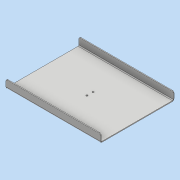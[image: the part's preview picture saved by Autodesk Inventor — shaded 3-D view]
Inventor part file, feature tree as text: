
AUTODESK INVENTOR PART (.ipt)
format: ipt  version: 2018 (Build 220112000, 112)  size: 156,160 bytes
history: native  units: mm
features: other x13, reference x6, sketch x3, hole x1
ambient origin geometry x8: Origin, YZ Plane, XZ Plane, XY Plane, X Axis, Y Axis, Z Axis, Center Point
bodies: Volumenkörper1 (feature_tree)
feature tree (23):
  other  "Fläche1"
  other  "Lasche1"
  hole  "Bohrung1"  [1 undecoded]
  other  "Eckenrundung1"
  sketch  "Skizze1"  dims[d0=230.0mm d1=180.0mm]
  other  "Grobblech1"
  sketch  "Skizze2"  dims[d2=2.0mm]
  other  "Grobblech2"
  other  "Biegung1"
  other  "Ecke1"
  sketch  "Skizze3"  dims[d3=2.0mm d4=1.0mm d5=4.0mm d6=2.0mm d7=20.0mm d8=90.0deg d9=2.0mm d10=8.0mm d11=2.0mm d12=2.0mm d13=3.0mm d14=4.0mm d15=6.0mm d16=4.0mm d17=2.0mm d18=90.0deg d19=2.0mm d20=20.594885mm]
  reference  "Referenz1"
  reference  "Referenz2"
  reference  "Referenz3"
  reference  "Referenz4"
  reference  "Referenz5"
  reference  "Referenz6"
  other  "Definition1"
  other  "<userpath>\Documents\Waage\CAD\Main.iam"
  other  "Main.iam"
  other  "LoadCell:2"
  other  "LoadCell:3"
  other  "LoadCell:1"
note: 1 required parameter value undecoded (feature->parameter linkage not recoverable at this tier; creation-order binding heuristic only, values carry confidence <= 0.55)
